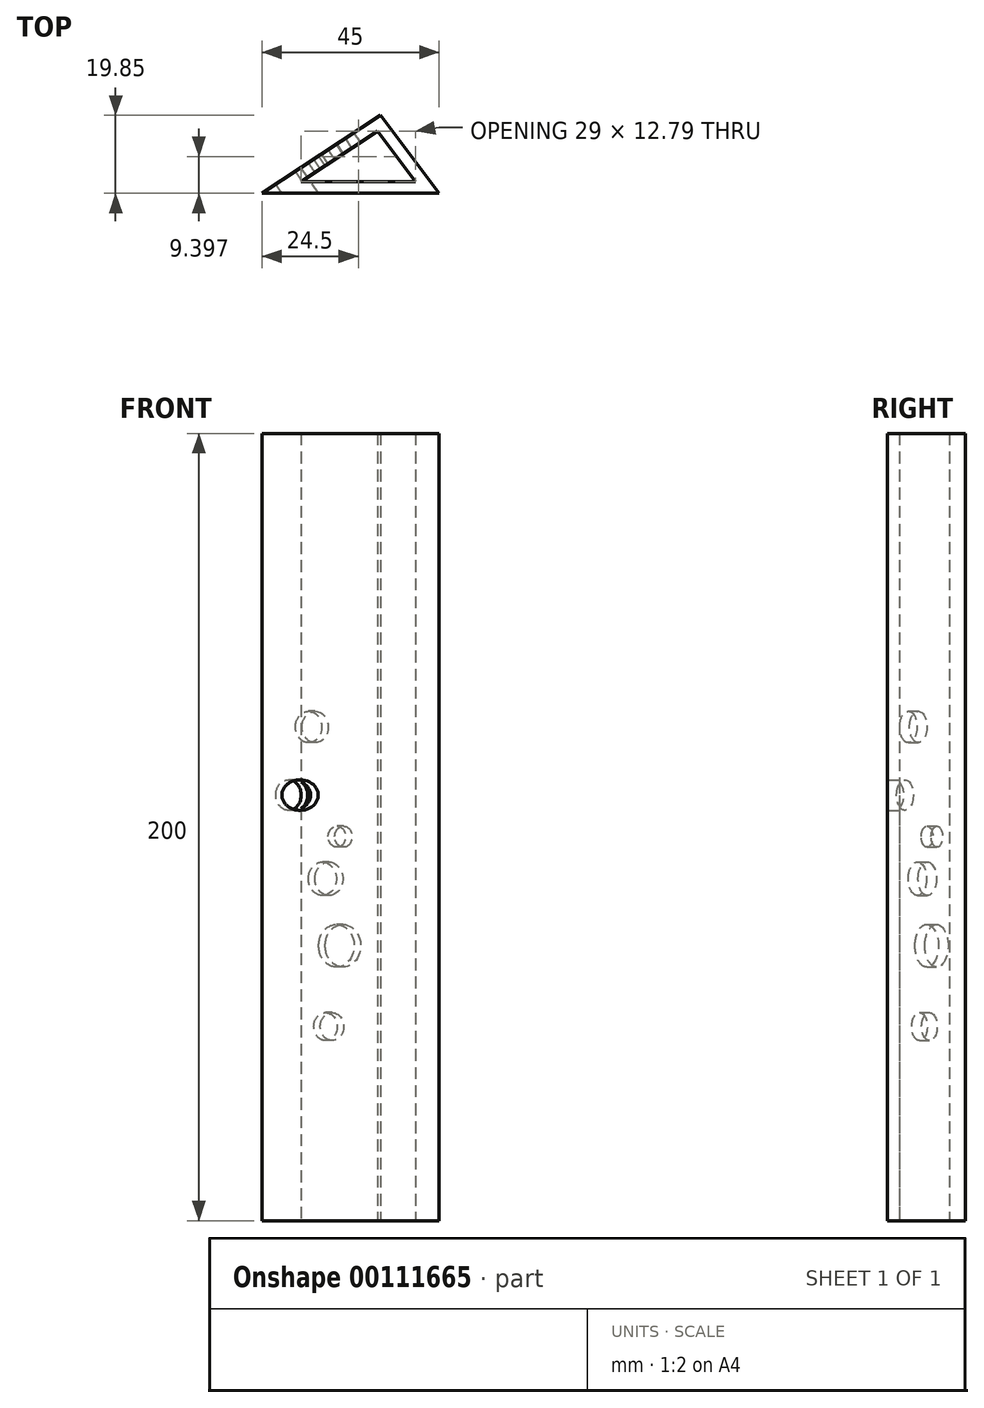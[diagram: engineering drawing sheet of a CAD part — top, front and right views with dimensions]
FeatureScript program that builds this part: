
annotation { "Feature Type Name" : "Feature", "Feature Type Description" : "" }
export const myFeature = defineFeature(function(context is Context, id is Id, definition is map)
    precondition{}
    {
        {
            var Q0;
            Q0=qCreatedBy(makeId("Top.planeOp"),FACE);
            var sketch = newSketch(context, id + "F0", { "sketchPlane" : qUnion([Q0])});
            skLineSegment(sketch, "E0.bottom", {"start": v(0, 0) * mm, "end": v(45, 0) * mm});
            skLineSegment(sketch, "E1", {"start": v(0, 0) * mm, "end": v(30.11, 19.85) * mm});
            skLineSegment(sketch, "E2", {"start": v(30.11, 19.85) * mm, "end": v(45, 0) * mm});
            skPoint(sketch, "E0.left.end.orphan", {"position": v(8.93, 27.45) * mm});
            skPoint(sketch, "E0.right.end.orphan", {"position": v(51.29, 12.26) * mm});
            skLineSegment(sketch, "E3.0", {"start": v(29.4, 15.8) * mm, "end": v(39, 3) * mm});
            skLineSegment(sketch, "E3.1", {"start": v(10, 3) * mm, "end": v(29.4, 15.8) * mm});
            skLineSegment(sketch, "E3.2", {"start": v(10, 3) * mm, "end": v(39, 3) * mm});
            skSolve(sketch);
        }
        {
            var Q0;
            Q0=makeQuery(id+"F0.imprint","IMPRINT",FACE,{"disambiguationData":[TD([[makeQuery(id+"F0.imprint","IMPRINT",EDGE,{"derivedFrom":sQuery(id+"F0.wireOp",EDGE,"E0.bottom")}),1.0]])]});
            extrude(context, id + "F1", {"entities" : qUnion([Q0]), "depth" : 200 * mm});
        }
        {
            var Q0;
            Q0=makeQuery(id+"F1.opExtrude","SWEPT_FACE",FACE,{"disambiguationData":[OSD([sQuery(id+"F0.wireOp",EDGE,"E1")])]});
            var sketch = newSketch(context, id + "F2", { "sketchPlane" : qUnion([Q0])});
            skCircle(sketch, "E4", {"center": v(-8.11, 108.13) * mm, "radius": 3.86 * mm});
            skCircle(sketch, "E5", {"center": v(-14.24, 125.43) * mm, "radius": 4 * mm});
            skCircle(sketch, "E6", {"center": v(-18.43, 86.86) * mm, "radius": 4.25 * mm});
            skCircle(sketch, "E7", {"center": v(-22.86, 97.56) * mm, "radius": 2.66 * mm});
            skCircle(sketch, "E8", {"center": v(-22.7, 69.85) * mm, "radius": 5.4 * mm});
            skCircle(sketch, "E9", {"center": v(-19.38, 49.3) * mm, "radius": 3.57 * mm});
            skSolve(sketch);
        }
        {
            var Q0;
            Q0 = qSketchRegion(id + "F2", true);
            extrude(context, id + "F3", {"entities" : qUnion([Q0]), "operationType" : NewBodyOperationType.REMOVE, "endBound" : BoundingType.UP_TO_NEXT, "oppositeDirection" : true, "depth" : 25 * mm});
        }
    });
